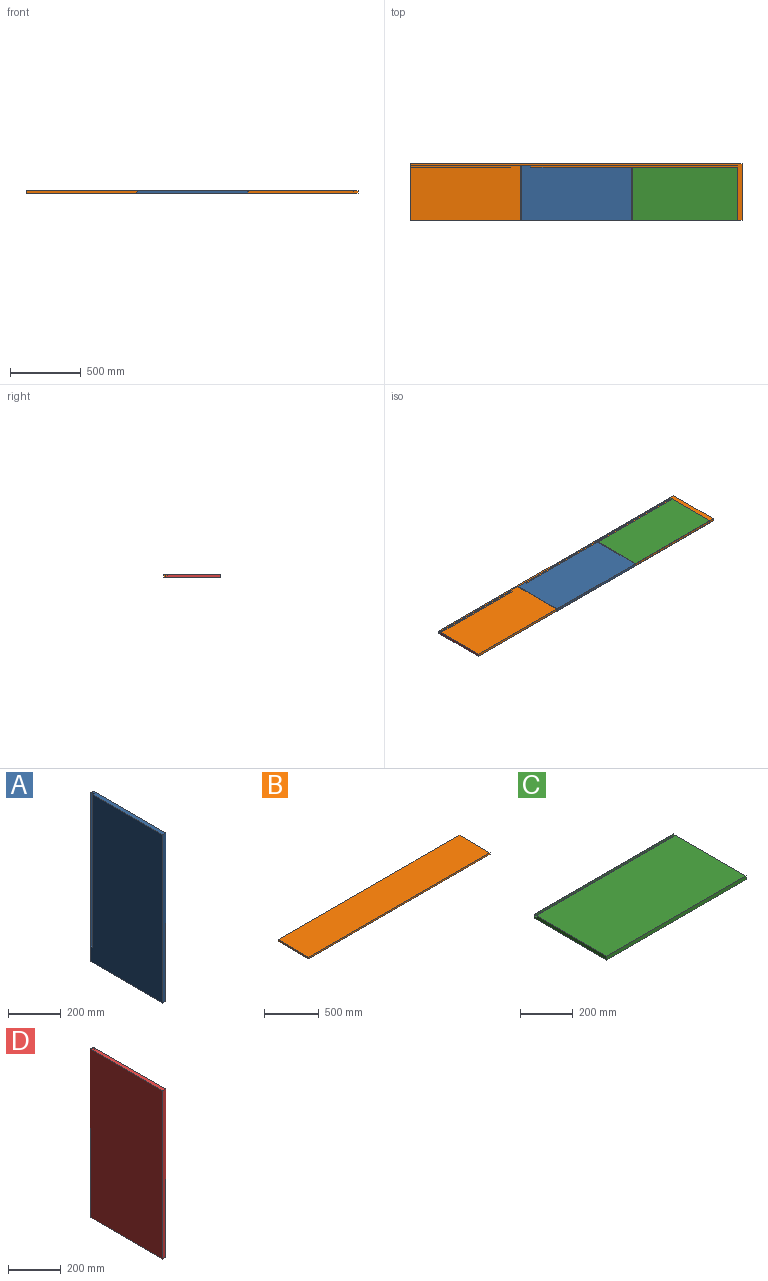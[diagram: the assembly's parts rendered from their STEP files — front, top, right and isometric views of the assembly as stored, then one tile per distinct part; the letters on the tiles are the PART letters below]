
ASSEMBLY  parts=4 mates=3
PART A: 10 faces, bbox 18x390x782 mm
  f0: plane 782x390mm, normal (-1,0,0), area 298216mm2, adj f1,f3,f4,f5,f6,f7,f8
  f1: plane 390x18mm, normal (0,0,1), area 6944mm2, adj f0,f2,f3,f4,f6,f8,f9
  f2: plane 782x390mm, normal (1,0,0), area 304980mm2, adj f1,f3,f4,f5
  f3: plane 782x18mm, normal (0,1,0), area 14076mm2, adj f0,f1,f2,f5
  f4: plane 782x18mm, normal (0,-1,0), area 14076mm2, adj f0,f1,f2,f5
  f5: plane 390x18mm, normal (0,0,-1), area 7020mm2, adj f0,f2,f3,f4
  f6: plane 712x8mm, normal (0,-1,0), area 5696mm2, adj f0,f1,f7,f9
  f7: plane 9.5x8mm, normal (0,0,1), area 76mm2, adj f0,f6,f8,f9
  f8: plane 712x8mm, normal (0,1,0), area 5696mm2, adj f0,f1,f7,f9
  f9: plane 712x9.5mm, normal (-1,0,0), area 6764mm2, adj f1,f6,f7,f8
PART B: 6 faces, bbox 2350x400x18 mm
  f0: plane 2350x18mm, normal (0,1,0), area 42300mm2, adj f1,f3,f4,f5
  f1: plane 400x18mm, normal (-1,0,0), area 7200mm2, adj f0,f2,f4,f5
  f2: plane 2350x18mm, normal (0,-1,0), area 42300mm2, adj f1,f3,f4,f5
  f3: plane 400x18mm, normal (1,0,0), area 7200mm2, adj f0,f2,f4,f5
  f4: plane 2350x400mm, normal (0,0,1), area 940000mm2, adj f0,f1,f2,f3
  f5: plane 2350x400mm, normal (0,0,-1), area 940000mm2, adj f0,f1,f2,f3
PART C: 10 faces, bbox 744x390x18 mm
  f0: plane 744x8mm, normal (0,1,0), area 5952mm2, adj f1,f7,f8,f9
  f1: plane 744x376.5mm, normal (0,0,1), area 280116mm2, adj f0,f2,f8,f9
  f2: plane 744x18mm, normal (0,-1,0), area 13392mm2, adj f1,f3,f8,f9
  f3: plane 744x390mm, normal (0,0,-1), area 290160mm2, adj f2,f4,f8,f9
  f4: plane 744x18mm, normal (0,1,0), area 13392mm2, adj f3,f5,f8,f9
  f5: plane 744x4mm, normal (0,0,1), area 2976mm2, adj f4,f6,f8,f9
  f6: plane 744x8mm, normal (0,-1,0), area 5952mm2, adj f5,f7,f8,f9
  f7: plane 744x9.5mm, normal (0,0,1), area 7068mm2, adj f0,f6,f8,f9
  f8: plane 390x18mm, normal (1,0,0), area 6944mm2, adj f0,f1,f2,f3,f4,f5,f6,f7
  f9: plane 390x18mm, normal (-1,0,0), area 6944mm2, adj f0,f1,f2,f3,f4,f5,f6,f7
PART D: 10 faces, bbox 18x390x782 mm
  f0: plane 390x18mm, normal (0,0,1), area 6944mm2, adj f1,f2,f3,f4,f6,f8,f9
  f1: plane 782x18mm, normal (0,1,0), area 14076mm2, adj f0,f2,f4,f5
  f2: plane 782x390mm, normal (-1,0,0), area 304980mm2, adj f0,f1,f3,f5
  f3: plane 782x18mm, normal (0,-1,0), area 14076mm2, adj f0,f2,f4,f5
  f4: plane 782x390mm, normal (1,0,0), area 298216mm2, adj f0,f1,f3,f5,f6,f7,f8
  f5: plane 390x18mm, normal (0,0,-1), area 7020mm2, adj f1,f2,f3,f4
  f6: plane 712x8mm, normal (0,1,0), area 5696mm2, adj f0,f4,f7,f9
  f7: plane 9.5x8mm, normal (0,0,1), area 76mm2, adj f4,f6,f8,f9
  f8: plane 712x8mm, normal (0,-1,0), area 5696mm2, adj f0,f4,f7,f9
  f9: plane 712x9.5mm, normal (1,0,0), area 6764mm2, adj f0,f6,f7,f8
PLACE A rot(axis=(0,1,0),90deg) t=(-389,-517.03,116.85)mm
PLACE B t=(1834.63,-363.07,-18)mm
PLACE C t=(397,180.26,-29.63)mm
PLACE D rot(axis=(0,-1,0),90deg) t=(-393,-524.77,28.74)mm
MATE fastened C.f1 <-> A.f0  axis (0,0,1) through (397,-200,0)mm
MATE fastened A.f0 <-> D.f4  axis (0,0,1) through (-389,-200,0)mm
MATE fastened D.f4 <-> B.f4  axis (0,0,1) through (-1175,-200,0)mm
